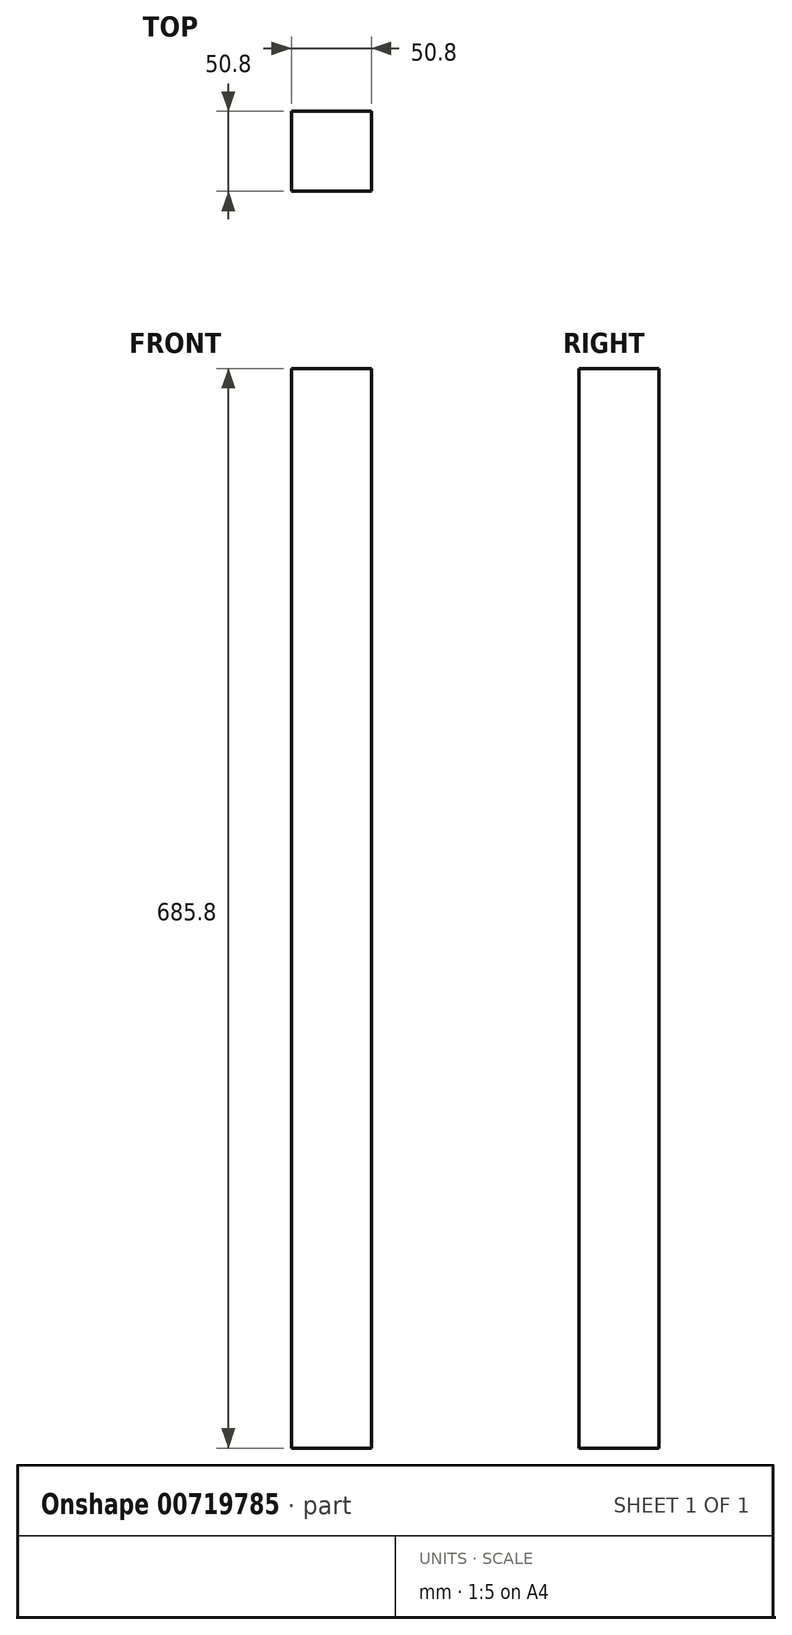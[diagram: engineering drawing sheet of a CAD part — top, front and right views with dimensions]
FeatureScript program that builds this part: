
annotation { "Feature Type Name" : "Feature", "Feature Type Description" : "" }
export const myFeature = defineFeature(function(context is Context, id is Id, definition is map)
    precondition{}
    {
        {
            var Q0;
            Q0=qCreatedBy(makeId("Top.planeOp"),FACE);
            var sketch = newSketch(context, id + "F0", { "sketchPlane" : qUnion([Q0])});
            skLineSegment(sketch, "E0.bottom", {"start": v(-134.56, -67.47) * mm, "end": v(-83.76, -67.47) * mm});
            skLineSegment(sketch, "E0.top", {"start": v(-134.56, -16.67) * mm, "end": v(-83.76, -16.67) * mm});
            skLineSegment(sketch, "E0.left", {"start": v(-134.56, -67.47) * mm, "end": v(-134.56, -16.67) * mm});
            skLineSegment(sketch, "E0.right", {"start": v(-83.76, -67.47) * mm, "end": v(-83.76, -16.67) * mm});
            skSolve(sketch);
        }
        {
            var Q0;
            Q0 = qSketchRegion(id + "F0", true);
            extrude(context, id + "F1", {"entities" : qUnion([Q0]), "depth" : 685.8 * mm, "offsetDistance" : 25.4 * mm});
        }
    });
